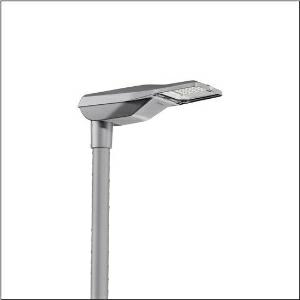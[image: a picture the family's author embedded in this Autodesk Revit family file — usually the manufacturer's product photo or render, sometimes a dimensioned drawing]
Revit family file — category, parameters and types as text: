
# Revit family: streetlight_sl_21_iq_micro___p0_8ab_5xe1r31g08cb_4e53
name_source: partatom
category: Lighting Fixtures
units: mm (PartAtom-declared; Revit-internal decimal feet)

## family parameters
Cut with Voids When Loaded = No
Host = Face
Light Source = No
Part Type = Normal
Room Calculation Point = No
Round Connector Dimension = Use Diameter
Shared = No

## types (1)
- --- (1 x LED, 2510 lm, 19.4 W, 3000K)
    Apparent Load = 19 VA
    CIE Flux Codes = 36 71 98 100 100
    Color Rendering = 70
    Color Temperature = 3000K
    Default Elevation = 1800 mm
    Description = Streetlight SL 21 iQ micro, mast luminaire, primary light control with lens, of PMMA, primary optical cover: cover, of toughened safety glass, transparent, light distribution: P0.8aB, light emission: direct distribution, primary light characteristic: asymmetric, installation type: post-top, side-entry, LED, High Power LED, rated luminous flux: 2.510lm, luminous efficacy: 129lm/W, light colour: 730, colour temperature: 3000K, control gear: iQ Street-Remote, control: pre-setting: linear dimming characteristic, Street-Remote, Auto-Match, Temp-Guard, Lumen-Switch, Night-Set, Smart-Wire, Light-Fading, Desk-Remote (wireless, voltage-free reading and setting of iQ features in the workshop via application-optimized NFC function/RFID function), optimised constant luminous flux control (CLO 2.0), mains connection: 220..240V, AC, 50/60Hz, start of lifetime: 19W, end of service life: 20W, reduction: 10W, luminaire housing, of diecast aluminium, powder-coated, Siteco® metallic grey (DB 702S), corrosivity category C5 mid according to DIN EN ISO 12944, please order mast flange separately, inclination adjustable: 0°, 5°, 10°, 15°, sealing non-destructively replaceable, multi-level sealing system, length: 528mm, width: 235mm, height: 110mm, mast flange for spigot size: 42mm (side-entry): 5XC10008XM4, 60/48mm (side-entry/post-top): 5XC10108XM2, 76/60mm (side-entry/post-top): 5XC10108XM1, protection rating (complete): IP66, insulation class (complete): insulation class II (safety insulation), certification: CE, ENEC, ENEC+, VDE, impact resistance: IK10, permissible operating ambient temperature for outdoor applications: -40..+50°C, standard-compliant lighting for roads and squares, packaging unit: 1 piece

Light Distribution: P0.8aB
    Height = 110 mm
    Lamp = 1 x LED
    Lamp Light Flux = 2510 lm
    Lamp Power = 19.4 W
    Lamp count = 1
    Length = 528 mm
    Luminous efficacy = 129 lm/W
    Manufacturer = Siteco
    ModVariant = No
    Model = 5XE1R31G08CB
    Number of Poles = 1
    OnlyDefault = Yes
    Power Factor = 1
    Product Name = Streetlight SL 21 iQ micro | P0.8aB
    Product group = mast luminaire | pylon top
    ProductGroupID = 6100
    Protection Class = Protection class II
    Protection Degree = IP 66
    RLX_Detail_Level = 1
    RLX_Emergency_Light_Flux = 0 lm
    RLX_Emergency_Type = 0
    RLX_Emergency_Type_DB = No
    RlxData = <blob elided: 99217 chars, md5=8684fdd5>
    Socket = socket
    Standby Power = 0 W
    System Light Flux = 2510 lm
    System Power = 19 W
    Type Comments = factory setting: luminous flux: 100 % | dim-lin: 254 | 387 mA
    Type Image = l_1006881.jpg
    URL = http://relux.com
    VarID = @adj_074712
    Voltage = 0 V
    Weight = 0.00 kg
    Width = 235 mm

## geometry (parser evidence)
native form markers: Blend x4, Sweep x10
no freeform markers — native parametric forms only
